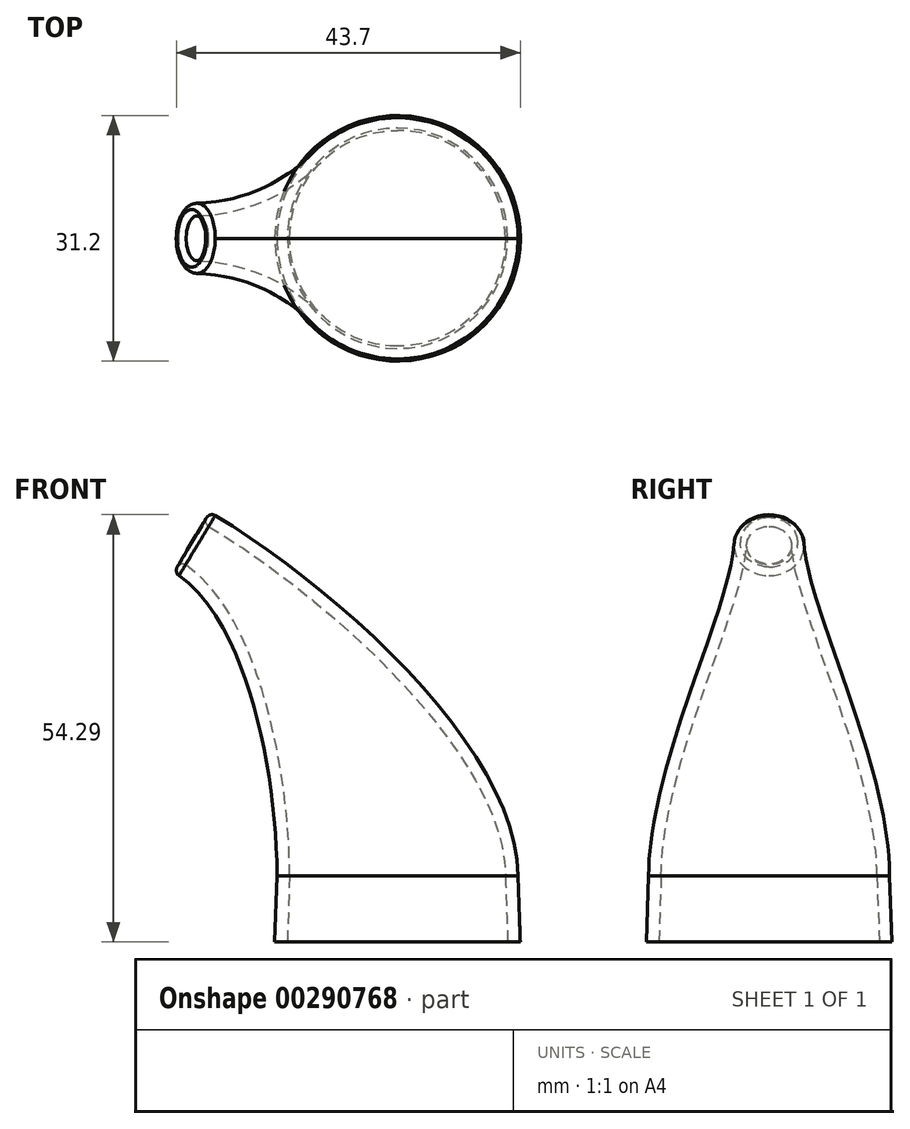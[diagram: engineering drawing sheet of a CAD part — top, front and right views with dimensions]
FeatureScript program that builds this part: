
annotation { "Feature Type Name" : "Feature", "Feature Type Description" : "" }
export const myFeature = defineFeature(function(context is Context, id is Id, definition is map)
    precondition{}
    {
        {
            var Q0;
            Q0=qCreatedBy(makeId("Top.planeOp"),FACE);
            var sketch = newSketch(context, id + "F0", { "sketchPlane" : qUnion([Q0])});
            skCircle(sketch, "E0", {"center": v(0, 0) * mm, "radius": 14 * mm});
            skCircle(sketch, "E1", {"center": v(0, 0) * mm, "radius": 15.6 * mm});
            skSolve(sketch);
        }
        {
            var Q0;
            Q0=makeQuery(id+"F0.imprint","IMPRINT",FACE,{"disambiguationData":[TD([[makeQuery(id+"F0.imprint","IMPRINT",EDGE,{"derivedFrom":sQuery(id+"F0.wireOp",EDGE,"E0")}),-1.0]])]});
            var Q1;
            Q1=makeQuery(id+"F0.imprint","IMPRINT",FACE,{"disambiguationData":[TD([[makeQuery(id+"F0.imprint","IMPRINT",EDGE,{"derivedFrom":sQuery(id+"F0.wireOp",EDGE,"E0")}),1.0]])]});
            extrude(context, id + "F1", {"entities" : qUnion([Q0, Q1]), "depth" : 8.4 * mm, "hasDraft" : true, "draftAngle" : 2 * degree, "draftPullDirection" : true});
        }
        {
            var Q0;
            Q0=qCreatedBy(makeId("Front.planeOp"),FACE);
            var sketch = newSketch(context, id + "F2", { "sketchPlane" : qUnion([Q0])});
            skLineSegment(sketch, "E2", {"start": v(-28.4, 46.96) * mm, "end": v(-23.84, 54.6) * mm});
            skSolve(sketch);
        }
        {
            var Q0;
            Q0=sQuery(id+"F2.wireOp",EDGE,"E2");
            var Q1;
            Q1=qCreatedBy(makeId("Top.planeOp"),FACE);
            cPlane(context, id + "F3", {"entities" : qUnion([Q0, Q1]), "cplaneType" : CPlaneType.LINE_ANGLE, "offset" : 25 * mm, "angle" : 0 * degree, "width" : 150 * mm, "height" : 150 * mm});
        }
        {
            var Q0;
            Q0=qCreatedBy(id+"F3.planeOp",FACE);
            var sketch = newSketch(context, id + "F4", { "sketchPlane" : qUnion([Q0])});
            skArc(sketch, "E3", {"start": v(0, 34.68) * mm, "mid": v(-3.14, 33.38) * mm, "end": v(-4.44, 30.24) * mm});
            skArc(sketch, "E4", {"start": v(0, 25.8) * mm, "mid": v(3.14, 27.1) * mm, "end": v(4.44, 30.24) * mm});
            skArc(sketch, "E5", {"start": v(-4.44, 30.24) * mm, "mid": v(-3.14, 27.1) * mm, "end": v(0, 25.8) * mm});
            skArc(sketch, "E6", {"start": v(4.44, 30.24) * mm, "mid": v(3.14, 33.38) * mm, "end": v(0, 34.68) * mm});
            skLineSegment(sketch, "E7", {"start": v(0, 25.8) * mm, "end": v(-4.44, 30.24) * mm, "construction": true});
            skLineSegment(sketch, "E8", {"start": v(0, 34.68) * mm, "end": v(-4.44, 30.24) * mm, "construction": true});
            skLineSegment(sketch, "E9", {"start": v(0, 34.68) * mm, "end": v(4.44, 30.24) * mm, "construction": true});
            skLineSegment(sketch, "E10", {"start": v(0, 25.8) * mm, "end": v(4.44, 30.24) * mm, "construction": true});
            skSolve(sketch);
        }
        {
            var Q0;
            Q0=makeQuery(id+"F1.opExtrude","CAP_FACE",FACE,{"disambiguationData":[OSD([sQuery(id+"F0.wireOp",EDGE,"E1")])],"isStart":false});
            var sketch = newSketch(context, id + "F5", { "sketchPlane" : qUnion([Q0])});
            skArc(sketch, "E11", {"start": v(0, 15.3) * mm, "mid": v(-10.82, 10.82) * mm, "end": v(-15.3, 0) * mm});
            skArc(sketch, "E12", {"start": v(0, -15.3) * mm, "mid": v(10.82, -10.82) * mm, "end": v(15.3, 0) * mm});
            skArc(sketch, "E13", {"start": v(15.3, 0) * mm, "mid": v(10.82, 10.82) * mm, "end": v(0, 15.3) * mm});
            skArc(sketch, "E14", {"start": v(-15.3, 0) * mm, "mid": v(-10.82, -10.82) * mm, "end": v(0, -15.3) * mm});
            skLineSegment(sketch, "E15", {"start": v(0, 15.3) * mm, "end": v(-15.3, 0) * mm, "construction": true});
            skLineSegment(sketch, "E16", {"start": v(-15.3, 0) * mm, "end": v(0, -15.3) * mm, "construction": true});
            skLineSegment(sketch, "E17", {"start": v(0, -15.3) * mm, "end": v(15.3, 0) * mm, "construction": true});
            skLineSegment(sketch, "E18", {"start": v(15.3, 0) * mm, "end": v(0, 15.3) * mm, "construction": true});
            skSolve(sketch);
        }
        {
            var Q1;
            Q1 = qSketchRegion(id + "F4", true);
            var Q2;
            Q2 = qSketchRegion(id + "F5", true);
            loft(context, id + "F6", {"operationType" : NewBodyOperationType.ADD, "startCondition" : LoftEndDerivativeType.NORMAL_TO_PROFILE, "startMagnitude" : 1, "endCondition" : LoftEndDerivativeType.NORMAL_TO_PROFILE, "endMagnitude" : 1, "sheetProfilesArray" : [{ "sheetProfileEntities" : qUnion([Q1]) }, { "sheetProfileEntities" : qUnion([Q2]) }]});
        }
        {
            var Q0;
            Q0=makeQuery(id+"F6.opLoft","CAP_FACE",FACE,{"disambiguationData":[OSD([makeQuery(id+"F4.imprint","IMPRINT",FACE,{"disambiguationData":[TD([[makeQuery(id+"F4.imprint","IMPRINT",EDGE,{"derivedFrom":sQuery(id+"F4.wireOp",EDGE,"E3")}),1.0]])]})])],"isStart":true});
            var Q1;
            Q1=makeQuery(id+"F1.opExtrude","CAP_FACE",FACE,{"disambiguationData":[OSD([sQuery(id+"F0.wireOp",EDGE,"E1")])],"isStart":true});
            shell(context, id + "F7", {"entities" : qUnion([Q0, Q1]), "thickness" : 1.6 * mm});
        }
        {
            var Q0;
            Q0=makeQuery(id+"F7.opShell","OFFSET_EDGE",EDGE,{"disambiguationData":[OSD([sQuery(id+"F4.wireOp",EDGE,"E3"),sQuery(id+"F4.wireOp",EDGE,"E4"),sQuery(id+"F4.wireOp",EDGE,"E5"),sQuery(id+"F4.wireOp",EDGE,"E6")])]});
            var Q1;
            Q1=makeQuery(id+"F6.opLoft","MID_CAP_EDGE",EDGE,{"disambiguationData":[OSD([sQuery(id+"F4.wireOp",EDGE,"E3"),sQuery(id+"F4.wireOp",EDGE,"E5"),sQuery(id+"F4.wireOp",EDGE,"E6")])],"capPos":0.0});
            fillet(context, id + "F8", {"entities" : qUnion([Q0, Q1]), "radius" : 0.8 * mm, "tangentPropagation" : true, "allowEdgeOverflow" : false});
        }
    });
